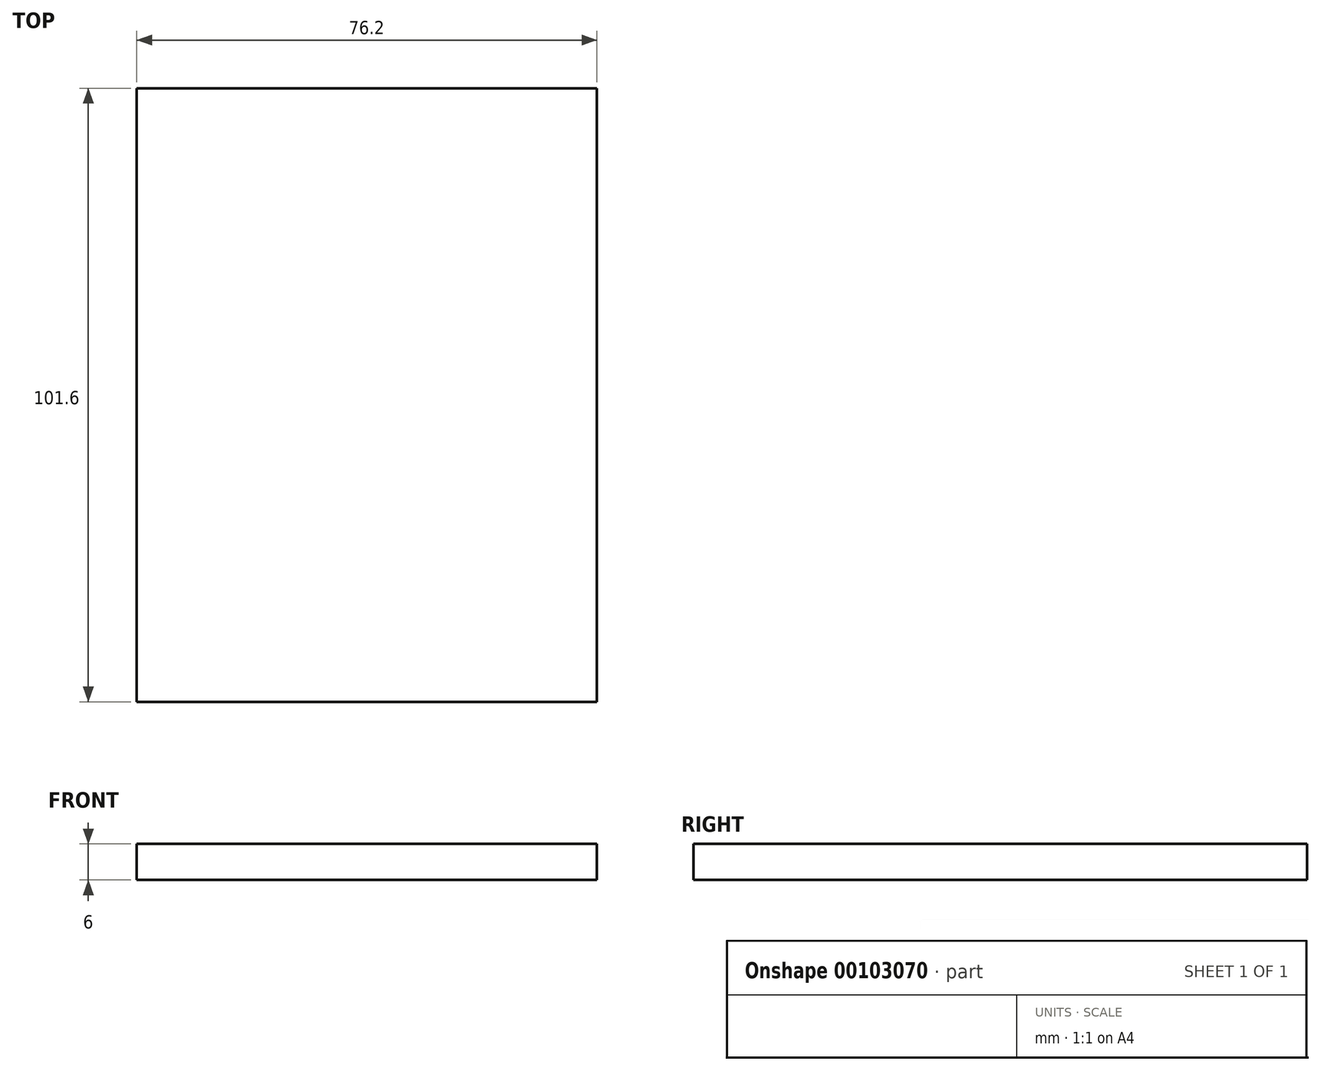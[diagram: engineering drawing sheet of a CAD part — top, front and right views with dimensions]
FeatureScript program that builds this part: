
annotation { "Feature Type Name" : "Feature", "Feature Type Description" : "" }
export const myFeature = defineFeature(function(context is Context, id is Id, definition is map)
    precondition{}
    {
        {
            var Q0;
            Q0=qCreatedBy(makeId("Top.planeOp"),FACE);
            var sketch = newSketch(context, id + "F0", { "sketchPlane" : qUnion([Q0])});
            skLineSegment(sketch, "E0.bottom", {"start": v(-94.2, 26.74) * mm, "end": v(-18, 26.74) * mm});
            skLineSegment(sketch, "E0.top", {"start": v(-94.2, -74.86) * mm, "end": v(-18, -74.86) * mm});
            skLineSegment(sketch, "E0.left", {"start": v(-94.2, 26.74) * mm, "end": v(-94.2, -74.86) * mm});
            skLineSegment(sketch, "E0.right", {"start": v(-18, 26.74) * mm, "end": v(-18, -74.86) * mm});
            skSolve(sketch);
        }
        {
            var Q0;
            Q0=makeQuery(id+"F0.imprint","IMPRINT",FACE,{"disambiguationData":[TD([[makeQuery(id+"F0.imprint","IMPRINT",EDGE,{"derivedFrom":sQuery(id+"F0.wireOp",EDGE,"E0.bottom")}),-1.0]])]});
            extrude(context, id + "F1", {"entities" : qUnion([Q0]), "endBound" : BoundingType.SYMMETRIC, "depth" : 6 * mm});
        }
    });
